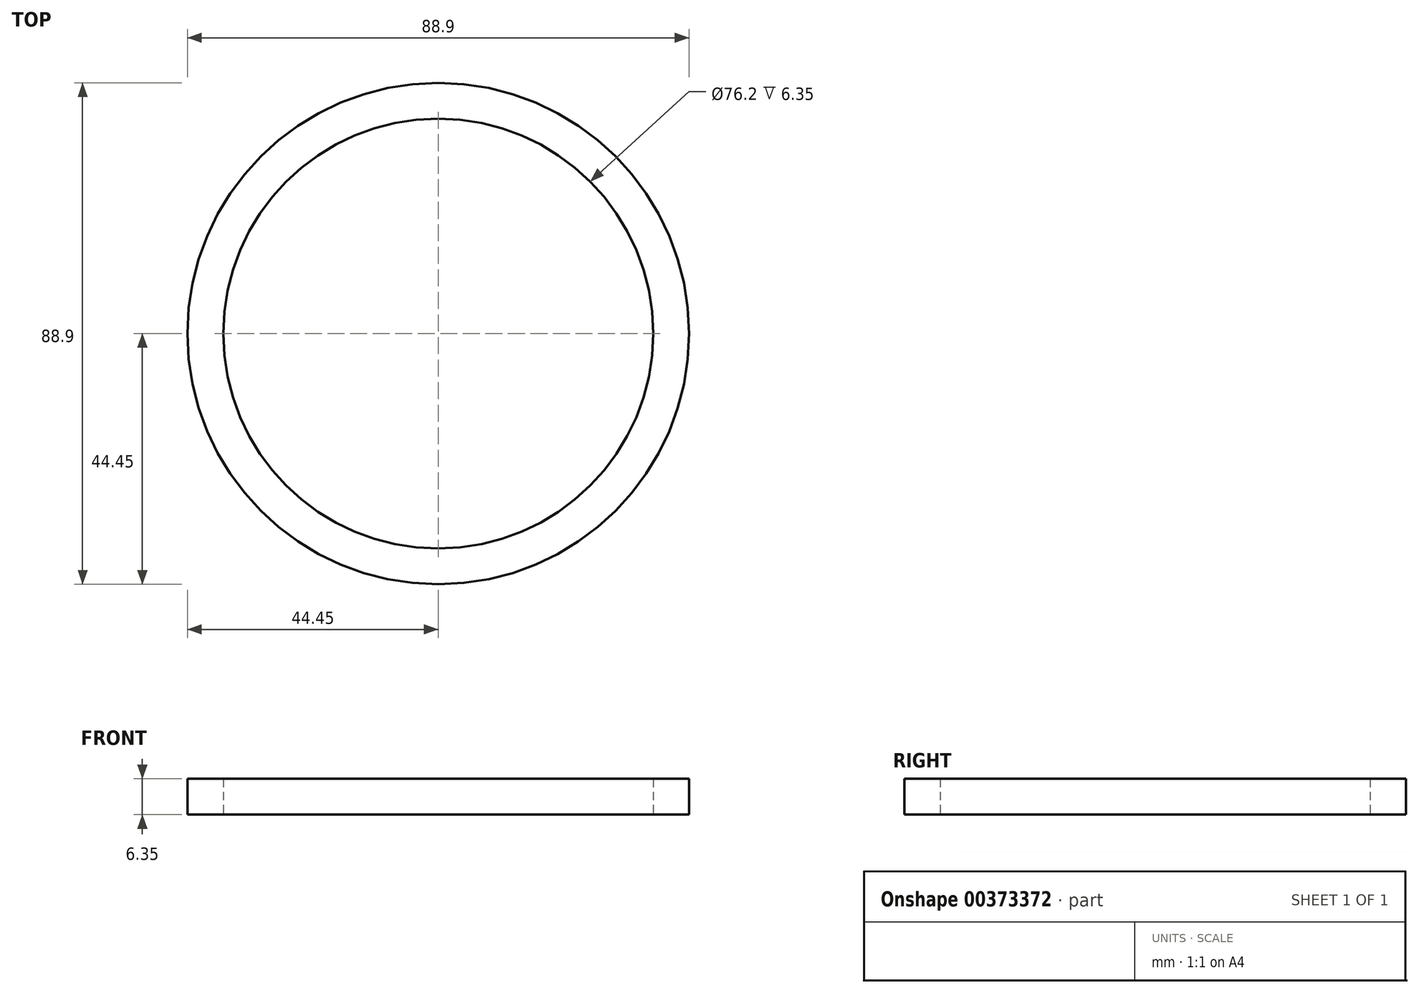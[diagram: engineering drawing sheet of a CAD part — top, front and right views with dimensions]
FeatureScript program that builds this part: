
annotation { "Feature Type Name" : "Feature", "Feature Type Description" : "" }
export const myFeature = defineFeature(function(context is Context, id is Id, definition is map)
    precondition{}
    {
        {
            var Q0;
            Q0=qCreatedBy(makeId("Top.planeOp"),FACE);
            var sketch = newSketch(context, id + "F0", { "sketchPlane" : qUnion([Q0])});
            skLineSegment(sketch, "E0", {"start": v(0, 0) * mm, "end": v(-26.94, -26.94) * mm});
            skLineSegment(sketch, "E1", {"start": v(0, 0) * mm, "end": v(26.94, -26.94) * mm});
            skLineSegment(sketch, "E2", {"start": v(0, 0) * mm, "end": v(0, 38.1) * mm});
            skCircle(sketch, "E3", {"center": v(0, 0) * mm, "radius": 38.1 * mm});
            skCircle(sketch, "E4", {"center": v(0, 0) * mm, "radius": 44.45 * mm});
            skSolve(sketch);
        }
        {
            var Q0;
            Q0=makeQuery(id+"F0.imprint","IMPRINT",FACE,{"disambiguationData":[TD([[makeQuery(id+"F0.imprint","IMPRINT",EDGE,{"derivedFrom":sQuery(id+"F0.wireOp",EDGE,"E4")}),1.0]])]});
            extrude(context, id + "F1", {"entities" : qUnion([Q0]), "depth" : 6.35 * mm});
        }
    });
